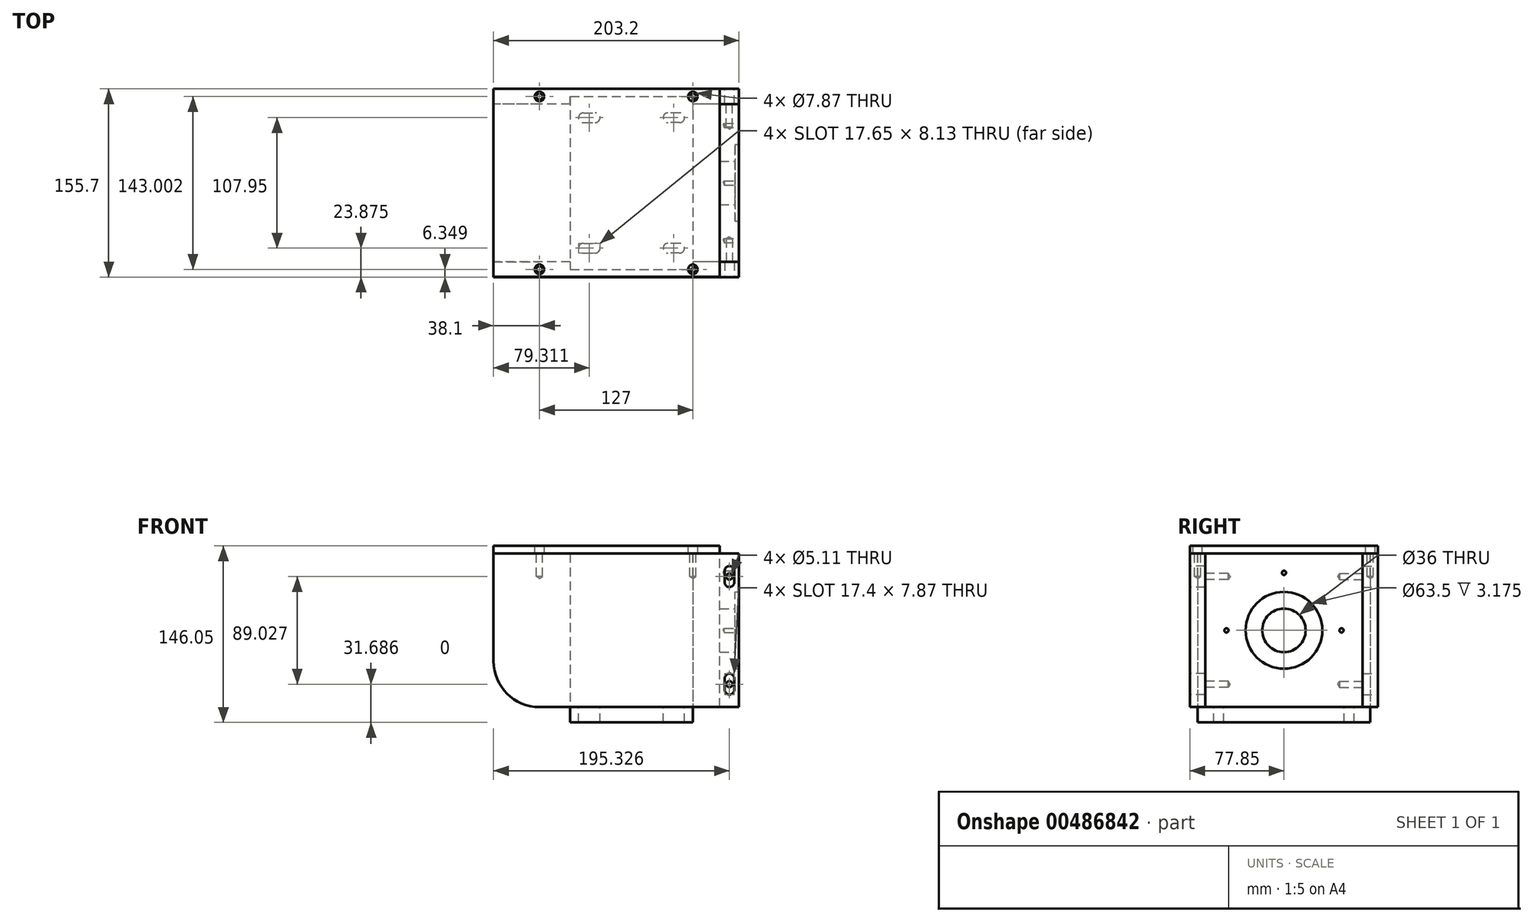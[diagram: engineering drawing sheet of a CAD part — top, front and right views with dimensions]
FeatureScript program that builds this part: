
annotation { "Feature Type Name" : "Feature", "Feature Type Description" : "" }
export const myFeature = defineFeature(function(context is Context, id is Id, definition is map)
    precondition{}
    {
        {
            var Q0;
            Q0=qCreatedBy(makeId("Top.planeOp"),FACE);
            var sketch = newSketch(context, id + "F0", { "sketchPlane" : qUnion([Q0])});
            skLineSegment(sketch, "E0.bottom", {"start": v(-50.8, 71.5) * mm, "end": v(50.8, 71.5) * mm});
            skLineSegment(sketch, "E0.top", {"start": v(-50.8, -71.5) * mm, "end": v(50.8, -71.5) * mm});
            skLineSegment(sketch, "E0.left", {"start": v(-50.8, 71.5) * mm, "end": v(-50.8, -71.5) * mm});
            skLineSegment(sketch, "E0.right", {"start": v(50.8, 71.5) * mm, "end": v(50.8, -71.5) * mm});
            skPoint(sketch, "E0.middle", {"position": v(0, 0) * mm});
            skLineSegment(sketch, "E1", {"start": v(0, 91.41) * mm, "end": v(0, -110.93) * mm, "construction": true});
            skPoint(sketch, "E1.endSnap0", {"position": v(0, 71.5) * mm});
            skLineSegment(sketch, "E2", {"start": v(-170.2, 0) * mm, "end": v(172.61, 0) * mm, "construction": true});
            skLineSegment(sketch, "E3.0", {"start": v(-34.93, 91.41) * mm, "end": v(-34.92, -110.93) * mm, "construction": true});
            skLineSegment(sketch, "E4", {"start": v(-34.92, -53.98) * mm, "end": v(-39.75, -53.98) * mm});
            skLineSegment(sketch, "E5", {"start": v(-39.75, -53.98) * mm, "end": v(-30.23, -53.98) * mm});
            skArc(sketch, "E6.0.startCap", {"start": v(-39.75, -58.04) * mm, "mid": v(-43.81, -53.98) * mm, "end": v(-39.75, -49.91) * mm});
            skArc(sketch, "E6.0.endCap", {"start": v(-30.23, -49.91) * mm, "mid": v(-26.16, -53.98) * mm, "end": v(-30.23, -58.04) * mm});
            skLineSegment(sketch, "E6.0.left", {"start": v(-39.75, -49.91) * mm, "end": v(-30.23, -49.91) * mm});
            skLineSegment(sketch, "E6.0.right", {"start": v(-39.75, -58.04) * mm, "end": v(-30.23, -58.04) * mm});
            skLineSegment(sketch, "E7.MirrorCS", {"start": v(39.75, -53.98) * mm, "end": v(30.23, -53.98) * mm});
            skLineSegment(sketch, "E8.MirrorCS", {"start": v(34.93, -53.98) * mm, "end": v(39.75, -53.97) * mm});
            skLineSegment(sketch, "E9.MirrorCS", {"start": v(39.75, -58.04) * mm, "end": v(30.23, -58.04) * mm});
            skLineSegment(sketch, "E10.MirrorCS", {"start": v(39.75, -49.91) * mm, "end": v(30.23, -49.91) * mm});
            skArc(sketch, "E11.MirrorCS", {"start": v(30.23, -49.91) * mm, "mid": v(26.16, -53.97) * mm, "end": v(30.23, -58.04) * mm});
            skArc(sketch, "E12.MirrorCS", {"start": v(39.75, -58.04) * mm, "mid": v(43.82, -53.98) * mm, "end": v(39.75, -49.91) * mm});
            skLineSegment(sketch, "E13.MirrorCS", {"start": v(50.8, -71.5) * mm, "end": v(-50.8, -71.5) * mm});
            skLineSegment(sketch, "E14.MirrorCS", {"start": v(-39.75, 53.97) * mm, "end": v(-30.23, 53.97) * mm});
            skLineSegment(sketch, "E15.MirrorCS", {"start": v(-34.92, 53.97) * mm, "end": v(-39.75, 53.97) * mm});
            skLineSegment(sketch, "E16.MirrorCS", {"start": v(-39.75, 58.04) * mm, "end": v(-30.23, 58.04) * mm});
            skLineSegment(sketch, "E17.MirrorCS", {"start": v(-39.75, 49.91) * mm, "end": v(-30.23, 49.91) * mm});
            skLineSegment(sketch, "E18.MirrorCS", {"start": v(39.75, 53.97) * mm, "end": v(30.23, 53.97) * mm});
            skLineSegment(sketch, "E19.MirrorCS", {"start": v(34.93, 53.97) * mm, "end": v(39.75, 53.97) * mm});
            skLineSegment(sketch, "E20.MirrorCS", {"start": v(39.75, 49.91) * mm, "end": v(30.23, 49.91) * mm});
            skArc(sketch, "E21.MirrorCS", {"start": v(39.75, 58.04) * mm, "mid": v(43.82, 53.97) * mm, "end": v(39.75, 49.91) * mm});
            skArc(sketch, "E22.MirrorCS", {"start": v(-30.23, 49.91) * mm, "mid": v(-26.16, 53.97) * mm, "end": v(-30.23, 58.04) * mm});
            skArc(sketch, "E23.MirrorCS", {"start": v(-39.75, 58.04) * mm, "mid": v(-43.81, 53.97) * mm, "end": v(-39.75, 49.91) * mm});
            skArc(sketch, "E24.MirrorCS", {"start": v(30.23, 49.91) * mm, "mid": v(26.16, 53.97) * mm, "end": v(30.23, 58.04) * mm});
            skLineSegment(sketch, "E25.MirrorCS", {"start": v(39.75, 58.04) * mm, "end": v(30.23, 58.04) * mm});
            skSolve(sketch);
        }
        {
            var Q0;
            Q0 = qSketchRegion(id + "F0", true);
            extrude(context, id + "F1", {"entities" : qUnion([Q0]), "oppositeDirection" : true, "depth" : 12.7 * mm});
        }
        {
            var Q0;
            Q0=makeQuery(id+"F1.opExtrude","CAP_FACE",FACE,{"disambiguationData":[OSD([sQuery(id+"F0.wireOp",EDGE,"E0.bottom"),sQuery(id+"F0.wireOp",EDGE,"E0.left"),sQuery(id+"F0.wireOp",EDGE,"E0.right"),sQuery(id+"F0.wireOp",EDGE,"E6.0.startCap"),sQuery(id+"F0.wireOp",EDGE,"E6.0.endCap"),sQuery(id+"F0.wireOp",EDGE,"E6.0.left"),sQuery(id+"F0.wireOp",EDGE,"E6.0.right"),sQuery(id+"F0.wireOp",EDGE,"E9.MirrorCS"),sQuery(id+"F0.wireOp",EDGE,"E10.MirrorCS"),sQuery(id+"F0.wireOp",EDGE,"E11.MirrorCS"),sQuery(id+"F0.wireOp",EDGE,"E12.MirrorCS"),sQuery(id+"F0.wireOp",EDGE,"E13.MirrorCS"),sQuery(id+"F0.wireOp",EDGE,"E16.MirrorCS"),sQuery(id+"F0.wireOp",EDGE,"E17.MirrorCS"),sQuery(id+"F0.wireOp",EDGE,"E20.MirrorCS"),sQuery(id+"F0.wireOp",EDGE,"E21.MirrorCS"),sQuery(id+"F0.wireOp",EDGE,"E22.MirrorCS"),sQuery(id+"F0.wireOp",EDGE,"E23.MirrorCS"),sQuery(id+"F0.wireOp",EDGE,"E24.MirrorCS"),sQuery(id+"F0.wireOp",EDGE,"E25.MirrorCS")])],"isStart":true});
            var sketch = newSketch(context, id + "F2", { "sketchPlane" : qUnion([Q0])});
            skLineSegment(sketch, "E26.0", {"start": v(88.9, -65.15) * mm, "end": v(88.9, -77.85) * mm});
            skLineSegment(sketch, "E27.0", {"start": v(-114.3, -65.15) * mm, "end": v(-114.3, -77.85) * mm});
            skLineSegment(sketch, "E28.0", {"start": v(50.8, -71.5) * mm, "end": v(-50.8, -71.5) * mm, "construction": true});
            skLineSegment(sketch, "E29.0", {"start": v(88.9, -65.15) * mm, "end": v(-114.3, -65.15) * mm});
            skLineSegment(sketch, "E30.0", {"start": v(88.9, -77.85) * mm, "end": v(-114.3, -77.85) * mm});
            skSolve(sketch);
        }
        {
            var Q0;
            {var subQ5=sQuery(id+"F2.wireOp",EDGE,"E26.0");Q0=makeQuery(id+"F2.imprint","IMPRINT",FACE,{"disambiguationData":[TD([[makeQuery(id+"F2.imprint","IMPRINT",EDGE,{"derivedFrom":subQ5}),-1.0]])]});}
            var Q1;
            {var subQ5=makeQuery(id+"F1.opExtrude","CAP_EDGE",EDGE,{"disambiguationData":[OSD([sQuery(id+"F0.wireOp",EDGE,"E13.MirrorCS")])],"isStart":true});Q1=makeQuery(id+"F2.imprint","IMPRINT",FACE,{"disambiguationData":[TD([[makeQuery(id+"F2.imprint","IMPRINT",EDGE,{"derivedFrom":subQ5}),-1.0]])]});}
            extrude(context, id + "F3", {"entities" : qUnion([Q0, Q1]), "depth" : 127 * mm});
        }
        {
            var Q0;
            Q0=makeQuery(id+"F3.opExtrude","CAP_FACE",FACE,{"disambiguationData":[OSD([sQuery(id+"F2.wireOp",EDGE,"E26.0"),sQuery(id+"F2.wireOp",EDGE,"E27.0"),sQuery(id+"F2.wireOp",EDGE,"E29.0"),sQuery(id+"F2.wireOp",EDGE,"E30.0")])],"isStart":false});
            var sketch = newSketch(context, id + "F4", { "sketchPlane" : qUnion([Q0])});
            skLineSegment(sketch, "E31.0", {"start": v(-12.7, -65.15) * mm, "end": v(-12.7, -77.85) * mm, "construction": true});
            skLineSegment(sketch, "E32.0", {"start": v(-76.2, -65.15) * mm, "end": v(-76.2, -77.85) * mm});
            skLineSegment(sketch, "E33.0", {"start": v(50.8, -65.15) * mm, "end": v(50.8, -77.85) * mm});
            skPoint(sketch, "E34", {"position": v(-76.2, -71.5) * mm});
            skPoint(sketch, "E35", {"position": v(50.8, -71.5) * mm});
            skSolve(sketch);
        }
        {
            var Q0;
            Q0=sQuery(id+"F4.wireOp",VERTEX,"E34");
            var Q1;
            Q1=sQuery(id+"F4.wireOp",VERTEX,"E35");
            var Q2;
            Q2=makeQuery(id+"F3.opExtrude","SWEPT_BODY",BODY,{"disambiguationData":[OSD([sQuery(id+"F2.wireOp",EDGE,"E26.0"),sQuery(id+"F2.wireOp",EDGE,"E27.0"),sQuery(id+"F2.wireOp",EDGE,"E29.0"),sQuery(id+"F2.wireOp",EDGE,"E30.0")])]});
            hole(context, id + "F5", {"style" : HoleStyle.SIMPLE, "endStyle" : HoleEndStyle.BLIND, "standardTappedOrClearance" : lookupTablePath({ "standard" : "ANSI", "engagement" : "75%", "pitch" : "20 tpi", "size" : "1/4", "type" : "Tapped" }), "standardBlindInLast" : lookupTablePath({ "standard" : "ANSI", "engagement" : "75%", "pitch" : "20 tpi", "size" : "1/4", "type" : "Tapped" }), "holeDiameter" : 5.1 * mm, "showTappedDepth" : true, "holeDepth" : 19.05 * mm, "isTappedThrough" : true, "tappedDepth" : 15.24 * mm, "tapClearance" : 3, "locations" : qUnion([Q0, Q1]), "scope" : qUnion([Q2]), "majorDiameter" : 6.35 * mm});
        }
        {
            var Q0;
            Q0=makeQuery(id+"F3.opExtrude","SWEPT_FACE",FACE,{"disambiguationData":[OSD([sQuery(id+"F2.wireOp",EDGE,"E30.0")])]});
            var sketch = newSketch(context, id + "F6", { "sketchPlane" : qUnion([Q0])});
            skLineSegment(sketch, "E36.0", {"start": v(88.9, 19.05) * mm, "end": v(81.03, 19.05) * mm, "construction": true});
            skLineSegment(sketch, "E37", {"start": v(-114.3, 63.5) * mm, "end": v(113.02, 63.5) * mm, "construction": true});
            skLineSegment(sketch, "E38", {"start": v(81.03, 19.05) * mm, "end": v(81.03, 14.22) * mm});
            skLineSegment(sketch, "E39", {"start": v(81.03, 14.22) * mm, "end": v(81.03, 23.75) * mm});
            skArc(sketch, "E40.0.startCap", {"start": v(84.96, 14.22) * mm, "mid": v(81.03, 10.29) * mm, "end": v(77.09, 14.22) * mm});
            skArc(sketch, "E40.0.endCap", {"start": v(77.09, 23.75) * mm, "mid": v(81.03, 27.69) * mm, "end": v(84.96, 23.75) * mm});
            skLineSegment(sketch, "E40.0.left", {"start": v(77.09, 14.22) * mm, "end": v(77.09, 23.75) * mm});
            skLineSegment(sketch, "E40.0.right", {"start": v(84.96, 14.22) * mm, "end": v(84.96, 23.75) * mm});
            skLineSegment(sketch, "E41.MirrorCS", {"start": v(81.03, 107.95) * mm, "end": v(81.03, 112.78) * mm});
            skLineSegment(sketch, "E42.MirrorCS", {"start": v(81.03, 112.78) * mm, "end": v(81.03, 103.25) * mm});
            skLineSegment(sketch, "E43.MirrorCS", {"start": v(84.96, 112.78) * mm, "end": v(84.96, 103.25) * mm});
            skLineSegment(sketch, "E44.MirrorCS", {"start": v(88.9, 107.95) * mm, "end": v(81.03, 107.95) * mm, "construction": true});
            skLineSegment(sketch, "E45.MirrorCS", {"start": v(77.09, 112.78) * mm, "end": v(77.09, 103.25) * mm});
            skArc(sketch, "E46.MirrorCS", {"start": v(77.09, 103.25) * mm, "mid": v(81.03, 99.31) * mm, "end": v(84.96, 103.25) * mm});
            skArc(sketch, "E47.MirrorCS", {"start": v(84.96, 112.78) * mm, "mid": v(81.03, 116.71) * mm, "end": v(77.09, 112.78) * mm});
            skSolve(sketch);
        }
        {
            var Q0;
            Q0 = qSketchRegion(id + "F6", true);
            extrude(context, id + "F7", {"entities" : qUnion([Q0]), "operationType" : NewBodyOperationType.REMOVE, "oppositeDirection" : true, "depth" : 25.4 * mm});
        }
        {
            var Q0;
            Q0=makeQuery(id+"F3.opExtrude","SWEPT_BODY",BODY,{"disambiguationData":[OSD([sQuery(id+"F2.wireOp",EDGE,"E26.0"),sQuery(id+"F2.wireOp",EDGE,"E27.0"),sQuery(id+"F2.wireOp",EDGE,"E29.0"),sQuery(id+"F2.wireOp",EDGE,"E30.0")])]});
            var Q1;
            Q1=qCreatedBy(makeId("Front.planeOp"),FACE);
            mirror(context, id + "F8", {"entities" : qUnion([Q0]), "mirrorPlane" : qUnion([Q1])});
        }
        {
            var Q0;
            Q0=makeQuery(id+"F8.opPattern","COPY",FACE,{"derivedFrom":makeQuery(id+"F3.opExtrude","CAP_FACE",FACE,{"disambiguationData":[OSD([sQuery(id+"F2.wireOp",EDGE,"E26.0"),sQuery(id+"F2.wireOp",EDGE,"E27.0"),sQuery(id+"F2.wireOp",EDGE,"E29.0"),sQuery(id+"F2.wireOp",EDGE,"E30.0")])],"isStart":false}),"instanceName":"1"});
            var sketch = newSketch(context, id + "F9", { "sketchPlane" : qUnion([Q0])});
            skLineSegment(sketch, "E48.bottom", {"start": v(-114.3, 77.85) * mm, "end": v(73.03, 77.85) * mm});
            skLineSegment(sketch, "E48.top", {"start": v(-114.3, -77.72) * mm, "end": v(73.03, -77.72) * mm});
            skLineSegment(sketch, "E48.left", {"start": v(-114.3, 77.85) * mm, "end": v(-114.3, -77.72) * mm});
            skLineSegment(sketch, "E48.right", {"start": v(73.02, 77.85) * mm, "end": v(73.02, -77.72) * mm});
            skSolve(sketch);
        }
        {
            var Q0;
            Q0 = qSketchRegion(id + "F9", true);
            extrude(context, id + "F10", {"entities" : qUnion([Q0]), "depth" : 6.35 * mm});
        }
        {
            var Q0;
            Q0=makeQuery(id+"F10.opExtrude","CAP_FACE",FACE,{"disambiguationData":[OSD([sQuery(id+"F9.wireOp",EDGE,"E48.bottom"),sQuery(id+"F9.wireOp",EDGE,"E48.top"),sQuery(id+"F9.wireOp",EDGE,"E48.left"),sQuery(id+"F9.wireOp",EDGE,"E48.right")])],"isStart":false});
            var sketch = newSketch(context, id + "F11", { "sketchPlane" : qUnion([Q0])});
            skCircle(sketch, "E49.0", {"center": v(-76.2, 71.5) * mm, "radius": 2.55 * mm, "construction": true});
            skCircle(sketch, "E50.0", {"center": v(50.8, 71.5) * mm, "radius": 2.55 * mm, "construction": true});
            skCircle(sketch, "E51.0", {"center": v(-76.2, -71.5) * mm, "radius": 2.55 * mm, "construction": true});
            skCircle(sketch, "E52.0", {"center": v(50.8, -71.5) * mm, "radius": 2.55 * mm, "construction": true});
            skSolve(sketch);
        }
        {
            var Q0;
            Q0=sQuery(id+"F11.wireOp",VERTEX,"E49.0.center");
            var Q1;
            Q1=sQuery(id+"F11.wireOp",VERTEX,"E50.0.center");
            var Q2;
            Q2=sQuery(id+"F11.wireOp",VERTEX,"E51.0.center");
            var Q3;
            Q3=sQuery(id+"F11.wireOp",VERTEX,"E52.0.center");
            var Q4;
            Q4=makeQuery(id+"F10.opExtrude","SWEPT_BODY",BODY,{"disambiguationData":[OSD([sQuery(id+"F9.wireOp",EDGE,"E48.bottom"),sQuery(id+"F9.wireOp",EDGE,"E48.top"),sQuery(id+"F9.wireOp",EDGE,"E48.left"),sQuery(id+"F9.wireOp",EDGE,"E48.right")])]});
            hole(context, id + "F12", {"style" : HoleStyle.SIMPLE, "endStyle" : HoleEndStyle.THROUGH, "holeDiameter" : 7.87 * mm, "isTappedThrough" : true, "tappedDepth" : 15.24 * mm, "tapClearance" : 3, "locations" : qUnion([Q0, Q1, Q2, Q3]), "scope" : qUnion([Q4])});
        }
        {
            var Q0;
            Q0=makeQuery(id+"F8.opPattern","COPY",FACE,{"derivedFrom":makeQuery(id+"F3.opExtrude","SWEPT_FACE",FACE,{"disambiguationData":[OSD([sQuery(id+"F2.wireOp",EDGE,"E29.0")])]}),"instanceName":"1"});
            var sketch = newSketch(context, id + "F13", { "sketchPlane" : qUnion([Q0])});
            skLineSegment(sketch, "E53.bottom", {"start": v(88.9, 0) * mm, "end": v(73.02, 0) * mm});
            skLineSegment(sketch, "E53.top", {"start": v(88.9, 127) * mm, "end": v(73.02, 127) * mm});
            skLineSegment(sketch, "E53.left", {"start": v(88.9, 0) * mm, "end": v(88.9, 127) * mm});
            skLineSegment(sketch, "E53.right", {"start": v(73.02, 0) * mm, "end": v(73.02, 127) * mm});
            skSolve(sketch);
        }
        {
            var Q0;
            Q0 = qSketchRegion(id + "F13", true);
            var Q1;
            Q1=makeQuery(id+"F3.opExtrude","SWEPT_FACE",FACE,{"disambiguationData":[OSD([sQuery(id+"F2.wireOp",EDGE,"E29.0")])]});
            extrude(context, id + "F14", {"entities" : qUnion([Q0]), "endBound" : BoundingType.UP_TO_SURFACE, "endBoundEntityFace" : qUnion([Q1]), "depth" : 25.4 * mm});
        }
        {
            var Q0;
            Q0=makeQuery(id+"F14.opExtrude","CAP_FACE",FACE,{"disambiguationData":[OSD([sQuery(id+"F13.wireOp",EDGE,"E53.bottom"),sQuery(id+"F13.wireOp",EDGE,"E53.top"),sQuery(id+"F13.wireOp",EDGE,"E53.left"),sQuery(id+"F13.wireOp",EDGE,"E53.right")])],"isStart":false});
            var sketch = newSketch(context, id + "F15", { "sketchPlane" : qUnion([Q0])});
            skLineSegment(sketch, "E54.0", {"start": v(81.03, 112.78) * mm, "end": v(81.03, 103.25) * mm, "construction": true});
            skLineSegment(sketch, "E55.0", {"start": v(81.03, 14.22) * mm, "end": v(81.03, 23.75) * mm, "construction": true});
            skPoint(sketch, "E56", {"position": v(81.03, 108.01) * mm});
            skPoint(sketch, "E57", {"position": v(81.03, 18.99) * mm});
            skSolve(sketch);
        }
        {
            var Q0;
            Q0=sQuery(id+"F15.wireOp",VERTEX,"E56");
            var Q1;
            Q1=sQuery(id+"F15.wireOp",VERTEX,"E57");
            var Q2;
            Q2=makeQuery(id+"F14.opExtrude","SWEPT_BODY",BODY,{"disambiguationData":[OSD([sQuery(id+"F13.wireOp",EDGE,"E53.bottom"),sQuery(id+"F13.wireOp",EDGE,"E53.top"),sQuery(id+"F13.wireOp",EDGE,"E53.left"),sQuery(id+"F13.wireOp",EDGE,"E53.right")])]});
            hole(context, id + "F16", {"style" : HoleStyle.SIMPLE, "endStyle" : HoleEndStyle.BLIND, "standardTappedOrClearance" : lookupTablePath({ "standard" : "ANSI", "engagement" : "75%", "pitch" : "20 tpi", "size" : "1/4", "type" : "Tapped" }), "standardBlindInLast" : lookupTablePath({ "standard" : "ANSI", "engagement" : "75%", "pitch" : "20 tpi", "size" : "1/4", "type" : "Tapped" }), "holeDiameter" : 5.1 * mm, "showTappedDepth" : true, "holeDepth" : 19.05 * mm, "isTappedThrough" : true, "tappedDepth" : 15.24 * mm, "tapClearance" : 3, "locations" : qUnion([Q0, Q1]), "scope" : qUnion([Q2]), "majorDiameter" : 6.35 * mm});
        }
        {
            var Q0;
            Q0=makeQuery(id+"F14.opExtrude","CAP_FACE",FACE,{"disambiguationData":[OSD([sQuery(id+"F13.wireOp",EDGE,"E53.bottom"),sQuery(id+"F13.wireOp",EDGE,"E53.top"),sQuery(id+"F13.wireOp",EDGE,"E53.left"),sQuery(id+"F13.wireOp",EDGE,"E53.right")])],"isStart":true});
            var sketch = newSketch(context, id + "F17", { "sketchPlane" : qUnion([Q0])});
            skLineSegment(sketch, "E58.0.0", {"start": v(-73.02, 127) * mm, "end": v(-73.02, 0) * mm, "construction": true});
            skLineSegment(sketch, "E58.0.1", {"start": v(-73.02, 0) * mm, "end": v(-88.9, 0) * mm, "construction": true});
            skLineSegment(sketch, "E58.0.2", {"start": v(-88.9, 0) * mm, "end": v(-88.9, 127) * mm, "construction": true});
            skLineSegment(sketch, "E58.0.3", {"start": v(-88.9, 127) * mm, "end": v(-73.02, 127) * mm, "construction": true});
            skCircle(sketch, "E59.0", {"center": v(-81.03, 108.01) * mm, "radius": 2.55 * mm, "construction": true});
            skCircle(sketch, "E60.0", {"center": v(-81.03, 18.99) * mm, "radius": 2.55 * mm, "construction": true});
            skSolve(sketch);
        }
        {
            var Q0;
            Q0=sQuery(id+"F17.wireOp",VERTEX,"E59.0.center");
            var Q1;
            Q1=sQuery(id+"F17.wireOp",VERTEX,"E60.0.center");
            var Q2;
            Q2=makeQuery(id+"F14.opExtrude","SWEPT_BODY",BODY,{"disambiguationData":[OSD([sQuery(id+"F13.wireOp",EDGE,"E53.bottom"),sQuery(id+"F13.wireOp",EDGE,"E53.top"),sQuery(id+"F13.wireOp",EDGE,"E53.left"),sQuery(id+"F13.wireOp",EDGE,"E53.right")])]});
            hole(context, id + "F18", {"style" : HoleStyle.SIMPLE, "endStyle" : HoleEndStyle.BLIND, "standardTappedOrClearance" : lookupTablePath({ "standard" : "ANSI", "engagement" : "75%", "pitch" : "20 tpi", "size" : "1/4", "type" : "Tapped" }), "standardBlindInLast" : lookupTablePath({ "standard" : "ANSI", "engagement" : "75%", "pitch" : "20 tpi", "size" : "1/4", "type" : "Tapped" }), "holeDiameter" : 5.1 * mm, "showTappedDepth" : true, "holeDepth" : 19.05 * mm, "isTappedThrough" : true, "tappedDepth" : 15.24 * mm, "tapClearance" : 3, "locations" : qUnion([Q0, Q1]), "scope" : qUnion([Q2]), "majorDiameter" : 6.35 * mm});
        }
        {
            var Q0;
            Q0=makeQuery(id+"F14.opExtrude","SWEPT_FACE",FACE,{"disambiguationData":[OSD([sQuery(id+"F13.wireOp",EDGE,"E53.left")])]});
            var sketch = newSketch(context, id + "F19", { "sketchPlane" : qUnion([Q0])});
            skLineSegment(sketch, "E61.0", {"start": v(-65.15, 127) * mm, "end": v(-65.15, 0) * mm, "construction": true});
            skLineSegment(sketch, "E62", {"start": v(-65.15, 63.5) * mm, "end": v(65.15, 63.5) * mm, "construction": true});
            skCircle(sketch, "E63", {"center": v(0, 63.5) * mm, "radius": 18 * mm});
            skSolve(sketch);
        }
        {
            var Q0;
            Q0 = qSketchRegion(id + "F19", true);
            extrude(context, id + "F20", {"entities" : qUnion([Q0]), "operationType" : NewBodyOperationType.REMOVE, "oppositeDirection" : true, "depth" : 25.4 * mm});
        }
        {
            var Q0;
            Q0=makeQuery(id+"F14.opExtrude","SWEPT_FACE",FACE,{"disambiguationData":[OSD([sQuery(id+"F13.wireOp",EDGE,"E53.left")])]});
            var sketch = newSketch(context, id + "F21", { "sketchPlane" : qUnion([Q0])});
            skCircle(sketch, "E64.0", {"center": v(0, 63.5) * mm, "radius": 18 * mm, "construction": true});
            skCircle(sketch, "E65", {"center": v(0, 63.5) * mm, "radius": 31.75 * mm});
            skSolve(sketch);
        }
        {
            var Q0;
            Q0 = qSketchRegion(id + "F21", true);
            extrude(context, id + "F22", {"entities" : qUnion([Q0]), "operationType" : NewBodyOperationType.REMOVE, "oppositeDirection" : true, "depth" : 3.17 * mm});
        }
        {
            var Q0;
            Q0=makeQuery(id+"F14.opExtrude","SWEPT_FACE",FACE,{"disambiguationData":[OSD([sQuery(id+"F13.wireOp",EDGE,"E53.left")])]});
            var sketch = newSketch(context, id + "F23", { "sketchPlane" : qUnion([Q0])});
            skCircle(sketch, "E66.0", {"center": v(0, 63.5) * mm, "radius": 31.75 * mm, "construction": true});
            skCircle(sketch, "E67", {"center": v(0, 63.5) * mm, "radius": 47.63 * mm, "construction": true});
            skLineSegment(sketch, "E68", {"start": v(0, 63.5) * mm, "end": v(0, 161.93) * mm, "construction": true});
            skPoint(sketch, "E69", {"position": v(0, 111.12) * mm});
            skPoint(sketch, "E70.1.0", {"position": v(-47.62, 63.5) * mm});
            skPoint(sketch, "E70.3.0", {"position": v(47.63, 63.5) * mm});
            skSolve(sketch);
        }
        {
            var Q0;
            Q0=sQuery(id+"F23.wireOp",VERTEX,"E69");
            var Q1;
            Q1=sQuery(id+"F23.wireOp",VERTEX,"E70.3.0");
            var Q2;
            Q2=sQuery(id+"F23.wireOp",VERTEX,"E70.1.0");
            var Q3;
            Q3=makeQuery(id+"F14.opExtrude","SWEPT_BODY",BODY,{"disambiguationData":[OSD([sQuery(id+"F13.wireOp",EDGE,"E53.bottom"),sQuery(id+"F13.wireOp",EDGE,"E53.top"),sQuery(id+"F13.wireOp",EDGE,"E53.left"),sQuery(id+"F13.wireOp",EDGE,"E53.right")])]});
            hole(context, id + "F24", {"style" : HoleStyle.SIMPLE, "endStyle" : HoleEndStyle.BLIND, "standardTappedOrClearance" : lookupTablePath({ "standard" : "ANSI", "engagement" : "75%", "pitch" : "32 tpi", "size" : "#8", "type" : "Tapped" }), "standardBlindInLast" : lookupTablePath({ "standard" : "ANSI", "engagement" : "75%", "pitch" : "32 tpi", "size" : "#8", "type" : "Tapped" }), "holeDiameter" : 3.45 * mm, "showTappedDepth" : true, "holeDepth" : 12.03 * mm, "isTappedThrough" : true, "tappedDepth" : 9.65 * mm, "tapClearance" : 3, "locations" : qUnion([Q0, Q1, Q2]), "scope" : qUnion([Q3]), "majorDiameter" : 4.17 * mm});
        }
        {
            var Q0;
            Q0=makeQuery(id+"F8.opPattern","COPY",EDGE,{"derivedFrom":makeQuery(id+"F3.opExtrude","CAP_EDGE",EDGE,{"disambiguationData":[OSD([sQuery(id+"F2.wireOp",EDGE,"E27.0")])],"isStart":true}),"instanceName":"1"});
            var Q1;
            Q1=makeQuery(id+"F3.opExtrude","CAP_EDGE",EDGE,{"disambiguationData":[OSD([sQuery(id+"F2.wireOp",EDGE,"E27.0")])],"isStart":true});
            fillet(context, id + "F25", {"entities" : qUnion([Q0, Q1]), "radius" : 38.1 * mm, "tangentPropagation" : true, "allowEdgeOverflow" : false});
        }
    });
